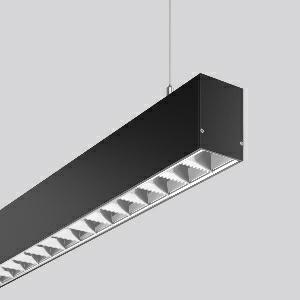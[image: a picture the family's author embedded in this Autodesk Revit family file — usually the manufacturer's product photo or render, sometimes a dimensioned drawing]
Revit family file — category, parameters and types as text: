
# Revit family: less_is_more_50_312338_003_76_73d5
name_source: partatom
category: Lighting Fixtures
units: mm (PartAtom-declared; Revit-internal decimal feet)

## family parameters
Cut with Voids When Loaded = No
Host = Face
Light Source = No
Part Type = Normal
Room Calculation Point = No
Round Connector Dimension = Use Diameter
Shared = No

## types (1)
- LESS IS MORE 50 (1 x LED Modul 830, 5050 lm, 3000)
    Apparent Load = 41 VA
    CIE Flux Codes = 95 100 100 100 100
    Color Rendering = 80
    Color Temperature = 3000
    Default Elevation = 1800 mm
    Description = Series: LESS IS MORE 50
Linear pendant luminaire for aesthetically sophisticated lighting. Housing: extruded aluminium profile, powder-coated. End cap aluminium powder-coated. Canopy made of aluminium, powder-coated. Alea optical system: Reflector structure (ABS, Aluminium-coated, highly polished) with integrated diffuser made of non-yellowing plastic (PMMA) opal for glare-free light at the workstation (screen-compliant according to EN 12464-1). Direct light emission. Suitable for pendant. 2-point steel cable suspension freely positionable and infinitely height-adjustable. Special lengths available on request. LED unit with integrated converter interchangeable and removable. Suitable for through-wiring. With sensors or as a safety luminaire on request. 
Colour: deep black, matt (RAL 9005)
Length: 1687 mm
Width: 57 mm
Height: 75 mm
Suspension length: 2000 mm
Lamp: LED
Socket: without socket
Colour temperature: 3000K
Colour rendering index (CRI): 80
System power: 41 W
Rated luminous flux: 5050 lm
Luminous efficiency: 123 lm/W
Control gear: Converter, dimmable, DALI
Protection class: I
Type of protection: IP 20
    Height = 75 mm
    Lamp = 1 x LED Modul 830
    Lamp Light Flux = 5050 lm
    Lamp count = 1
    Length = 1687 mm
    Lifetime = 50000 h
    Luminous efficacy = 123 lm/W
    Manufacturer = RZB
    ModVariant = No
    Model = 312338.003.76
    Mounting Place = Ceiling
    Mounting Type = Pendant
    Number of Poles = 1
    OnlyDefault = Yes
    Power Factor = 1
    Product Name = LESS IS MORE 50
    Product group = Pendant LED linear luminaires
    ProductGroupID = 907
    Protection Class = Protection class I
    Protection Degree = IP 20
    RLX_Detail_Level = 1
    RLX_Emergency_Light_Flux = 0 lm
    RLX_Emergency_Type = 0
    RLX_Emergency_Type_DB = No
    RlxData = <blob elided: 39501 chars, md5=e252bc45>
    Socket = socket
    Standby Power = 0 W
    System Light Flux = 5050 lm
    System Power = 41 W
    Type Comments = Product without accessories
    Type Image = 312342.003.jpg
    URL = http://relux.com
    VarID = ---
    Voltage = 230 V
    Voltage Range = 220-240 V
    Weight = 0.00 kg
    Width = 57 mm

## geometry (parser evidence)
native form markers: Blend x4, Sweep x9
no freeform markers — native parametric forms only
